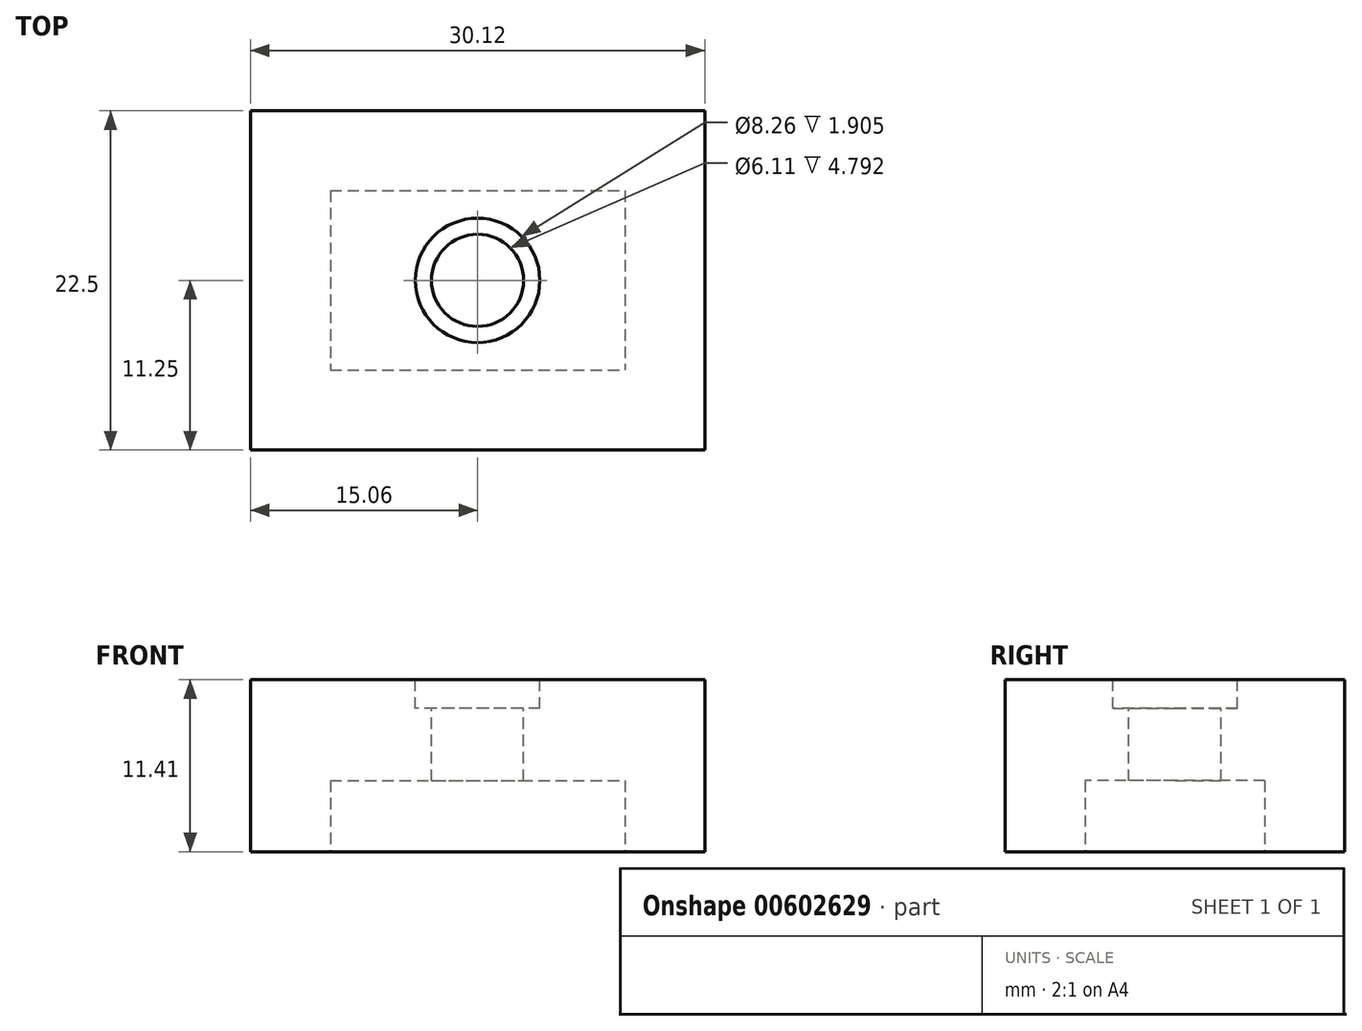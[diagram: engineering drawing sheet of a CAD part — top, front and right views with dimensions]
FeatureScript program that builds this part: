
annotation { "Feature Type Name" : "Feature", "Feature Type Description" : "" }
export const myFeature = defineFeature(function(context is Context, id is Id, definition is map)
    precondition{}
    {
        {
            var Q0;
            Q0=qCreatedBy(makeId("Top.planeOp"),FACE);
            var sketch = newSketch(context, id + "F0", { "sketchPlane" : qUnion([Q0])});
            skLineSegment(sketch, "E0.bottom", {"start": v(-15.06, -11.25) * mm, "end": v(15.06, -11.25) * mm});
            skLineSegment(sketch, "E0.top", {"start": v(-15.06, 11.25) * mm, "end": v(15.06, 11.25) * mm});
            skLineSegment(sketch, "E0.left", {"start": v(-15.06, -11.25) * mm, "end": v(-15.06, 11.25) * mm});
            skLineSegment(sketch, "E0.right", {"start": v(15.06, -11.25) * mm, "end": v(15.06, 11.25) * mm});
            skPoint(sketch, "E0.middle", {"position": v(0, 0) * mm});
            skSolve(sketch);
        }
        {
            var Q0;
            Q0=makeQuery(id+"F0.imprint","IMPRINT",FACE,{"disambiguationData":[TD([[makeQuery(id+"F0.imprint","IMPRINT",EDGE,{"derivedFrom":sQuery(id+"F0.wireOp",EDGE,"E0.bottom")}),1.0]])]});
            extrude(context, id + "F1", {"entities" : qUnion([Q0]), "oppositeDirection" : true, "depth" : 11.4 * mm, "offsetDistance" : 25.4 * mm});
        }
        {
            var Q0;
            Q0=makeQuery(id+"F1.opExtrude","CAP_FACE",FACE,{"disambiguationData":[OSD([sQuery(id+"F0.wireOp",EDGE,"E0.bottom"),sQuery(id+"F0.wireOp",EDGE,"E0.top"),sQuery(id+"F0.wireOp",EDGE,"E0.left"),sQuery(id+"F0.wireOp",EDGE,"E0.right")])],"isStart":false});
            var sketch = newSketch(context, id + "F2", { "sketchPlane" : qUnion([Q0])});
            skLineSegment(sketch, "E1.bottom", {"start": v(-9.76, -5.96) * mm, "end": v(9.77, -5.96) * mm});
            skLineSegment(sketch, "E1.top", {"start": v(-9.77, 5.96) * mm, "end": v(9.76, 5.96) * mm});
            skLineSegment(sketch, "E1.left", {"start": v(-9.77, -5.96) * mm, "end": v(-9.77, 5.96) * mm});
            skLineSegment(sketch, "E1.right", {"start": v(9.77, -5.96) * mm, "end": v(9.76, 5.96) * mm});
            skPoint(sketch, "E1.middle", {"position": v(0, 0) * mm});
            skSolve(sketch);
        }
        {
            var Q0;
            Q0=makeQuery(id+"F2.imprint","IMPRINT",FACE,{"disambiguationData":[TD([[makeQuery(id+"F2.imprint","IMPRINT",EDGE,{"derivedFrom":sQuery(id+"F2.wireOp",EDGE,"E1.bottom")}),1.0]])]});
            extrude(context, id + "F3", {"entities" : qUnion([Q0]), "operationType" : NewBodyOperationType.REMOVE, "oppositeDirection" : true, "depth" : 4.7 * mm, "offsetDistance" : 25.4 * mm});
        }
        {
            var Q0;
            Q0=makeQuery(id+"F1.opExtrude","CAP_FACE",FACE,{"disambiguationData":[OSD([sQuery(id+"F0.wireOp",EDGE,"E0.bottom"),sQuery(id+"F0.wireOp",EDGE,"E0.top"),sQuery(id+"F0.wireOp",EDGE,"E0.left"),sQuery(id+"F0.wireOp",EDGE,"E0.right")])],"isStart":true});
            var sketch = newSketch(context, id + "F4", { "sketchPlane" : qUnion([Q0])});
            skCircle(sketch, "E2", {"center": v(0, 0) * mm, "radius": 4.13 * mm});
            skSolve(sketch);
        }
        {
            var Q0;
            Q0=makeQuery(id+"F4.imprint","IMPRINT",FACE,{"disambiguationData":[TD([[makeQuery(id+"F4.imprint","IMPRINT",EDGE,{"derivedFrom":sQuery(id+"F4.wireOp",EDGE,"E2")}),1.0]])]});
            extrude(context, id + "F5", {"entities" : qUnion([Q0]), "operationType" : NewBodyOperationType.REMOVE, "oppositeDirection" : true, "depth" : 1.9 * mm, "offsetDistance" : 25.4 * mm});
        }
        {
            var Q0;
            Q0=makeQuery(id+"F5.boolean.opBoolean","COPY",FACE,{"derivedFrom":makeQuery(id+"F5.opExtrude","CAP_FACE",FACE,{"disambiguationData":[OSD([sQuery(id+"F4.wireOp",EDGE,"E2")])],"isStart":false})});
            var sketch = newSketch(context, id + "F6", { "sketchPlane" : qUnion([Q0])});
            skCircle(sketch, "E3", {"center": v(0, 0) * mm, "radius": 3.06 * mm});
            skSolve(sketch);
        }
        {
            var Q0;
            Q0=makeQuery(id+"F6.imprint","IMPRINT",FACE,{"disambiguationData":[TD([[makeQuery(id+"F6.imprint","IMPRINT",EDGE,{"derivedFrom":sQuery(id+"F6.wireOp",EDGE,"E3")}),1.0]])]});
            extrude(context, id + "F7", {"entities" : qUnion([Q0]), "operationType" : NewBodyOperationType.REMOVE, "oppositeDirection" : true, "depth" : 6.07 * mm, "offsetDistance" : 25.4 * mm});
        }
    });
